# Revit family: Doors_Swing_Avanti_Systems_Movare-Swing-Door
name_source: partatom
category: Doors
revit_build: Autodesk Revit 2015 (Build: 20140606_1530(x64)
units: mm (PartAtom-declared; Revit-internal decimal feet)

## types (8) — shared parameters
Acoustic performance (dB) = 42
Analytic Construction = <None>
Blinds material = Polyester powder - Avanti - White aluminium METALLIC - RAL9006
Description = Movare™ Movable Double Glazed Glass Partitions
Door Integrations = Pivot Glass Doors, Full Height Pass Door, End panels can be free swing pivot door access.
Door options = frameless pivot door
Flame spread = Class O Surface Spread of Flame
Frame Material = Polyester powder - Avanti - White aluminium METALLIC - RAL9006
Function = Interior
Glass Marker = Yes
Inset = 0' - 0 1/2"
LEED compatibility = LEED 2009 (v3): MRc3, MRc4, MRc5, MRc7, EQc4.2, EQc8.1 and EQc8.2. LEED v4: MRc1, MRc3, MRc4, MRc8, EQc2, EQc7 and EQc8.
Manufacturer = Avanti Systems USA
Maximum Height = 12' - 0"
Maximum Width = 5' - 0"
Offset = 0' - 0"
Product data url = https://bimobject.com
Sound Rating = 44
Thickness = 0' - 1 1/2"
URL = https://www.avantisystemsusa.com
Warranty = 1 year
box width = 6' - 0"

## per-type parameters (varying)
| type | Blinds | Blinds_vis | Flush Seal | Glazing Material | Hardware material | Model | Non Flush Seal | Type |
| Clear Tempered Seal Expanded | No | 0 | Yes | Glass - Avanti -  Clear Tempered | Stainless Steel - Avanti- Brushed Finish | Movare Double Glazed Swing Door Clear Tempered Seal Expanded | No | 2 |
| Clear Tempered | No | 0 | No | Glass - Avanti -  Clear Tempered | Stainless Steel - Avanti- Brushed Finish | Movare Double Glazed Swing Door Clear Tempered | Yes | 1 |
| Clear Laminated Seal Expanded | No | 0 | Yes | Glass - Avanti - Laminated Glass | Stainless Steel - Avanti- Brushed Finish | Movare Double Glazed Swing Door Clear Laminated Seal Expanded | No | 2 |
| Clear Laminated | No | 0 | No | Glass - Avanti - Laminated Glass | Stainless Steel - Avanti- Brushed Finish | Movare Double Glazed Swing Door Clear Laminated | Yes | 1 |
| Clear Tempered Seal Expanded with Blinds | Yes | 1 | Yes | Glass - Avanti -  Clear Tempered | Stainless Steel - Avanti- Brushed Finish | Movare Double Glazed Swing Door Clear Tempered Seal Expanded with Blinds | No | 2 |
| Clear Tempered with Blinds | Yes | 1 | No | Glass - Avanti -  Clear Tempered | Stainless Steel - Avanti- Brushed Finish | Movare Double Glazed Swing Door Clear Tempered with Blinds | Yes | 1 |
| Clear Laminated Seal Expanded with Blinds | Yes | 1 | Yes | Glass - Avanti - Laminated Glass | Stainless Steel - Avanti- Brushed Finish | Movare Double Glazed Swing Door Clear Laminated Seal Expanded with Blinds | No | 2 |
| Clear Laminated with Blinds | Yes | 1 | No | Glass - Avanti - Laminated Glass | Polyester powder - Avanti - White aluminium METALLIC - RAL9006 | Movare Double Glazed Swing Door Clear Laminated with Blinds | Yes | 1 |

## geometry (parser evidence)
native form markers: Sweep x18
no freeform markers — native parametric forms only
